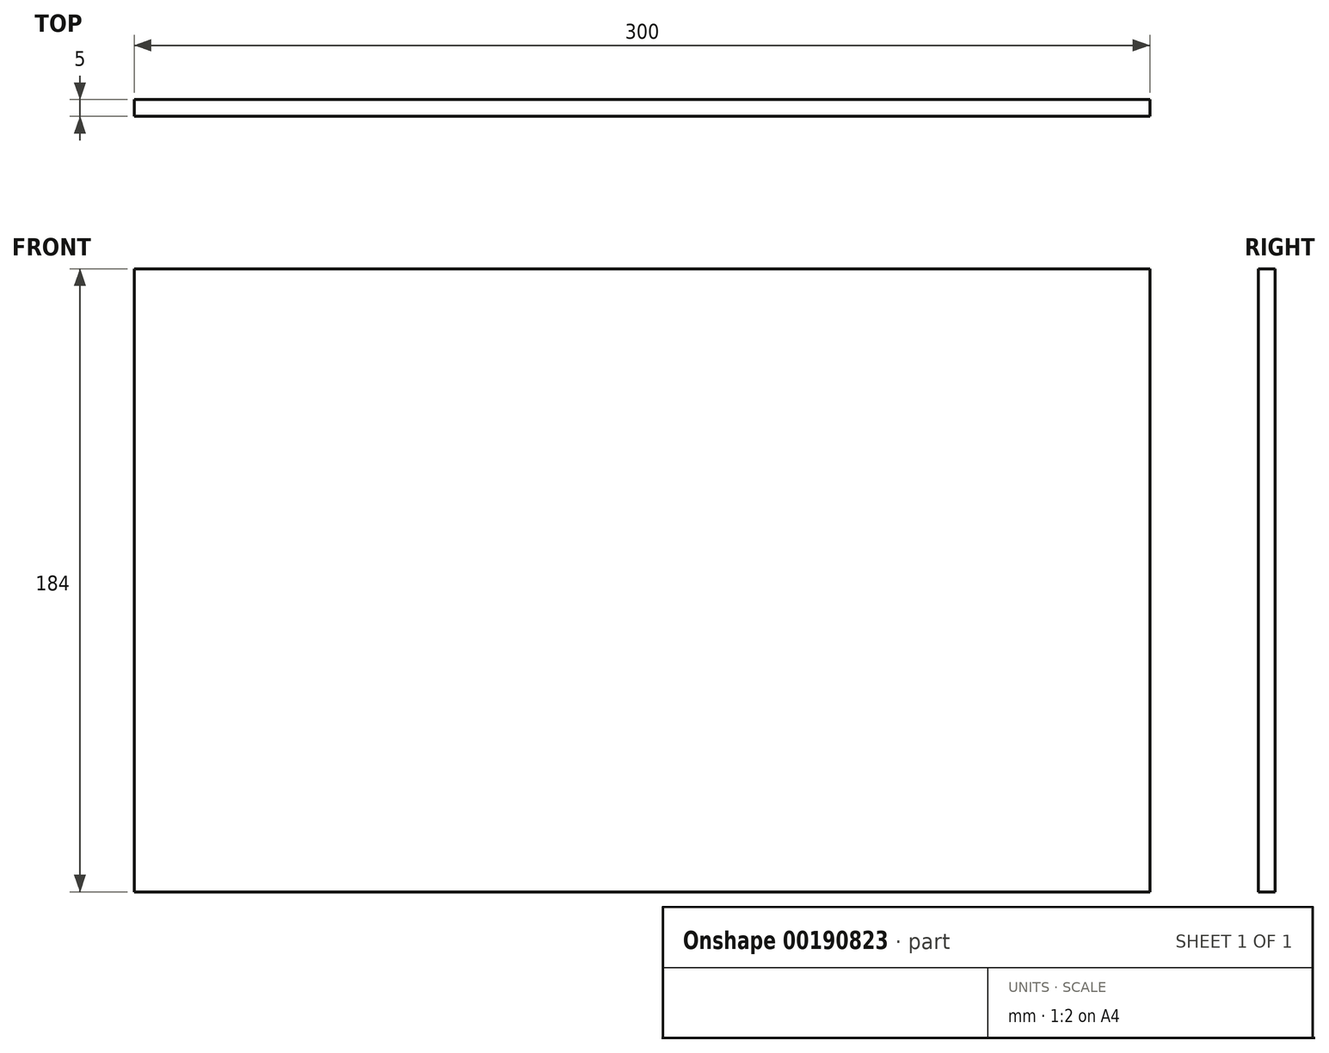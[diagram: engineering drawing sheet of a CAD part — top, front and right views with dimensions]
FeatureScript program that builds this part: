
annotation { "Feature Type Name" : "Feature", "Feature Type Description" : "" }
export const myFeature = defineFeature(function(context is Context, id is Id, definition is map)
    precondition{}
    {
        {
            var Q0;
            Q0=qCreatedBy(makeId("Front.planeOp"),FACE);
            var sketch = newSketch(context, id + "F0", { "sketchPlane" : qUnion([Q0])});
            skLineSegment(sketch, "E0.bottom", {"start": v(150, 92) * mm, "end": v(-150, 92) * mm});
            skLineSegment(sketch, "E0.top", {"start": v(150, -92) * mm, "end": v(-150, -92) * mm});
            skLineSegment(sketch, "E0.left", {"start": v(150, 92) * mm, "end": v(150, -92) * mm});
            skLineSegment(sketch, "E0.right", {"start": v(-150, 92) * mm, "end": v(-150, -92) * mm});
            skPoint(sketch, "E0.middle", {"position": v(0, 0) * mm});
            skSolve(sketch);
        }
        {
            var Q0;
            Q0 = qSketchRegion(id + "F0", true);
            extrude(context, id + "F1", {"entities" : qUnion([Q0]), "depth" : 5 * mm});
        }
    });
